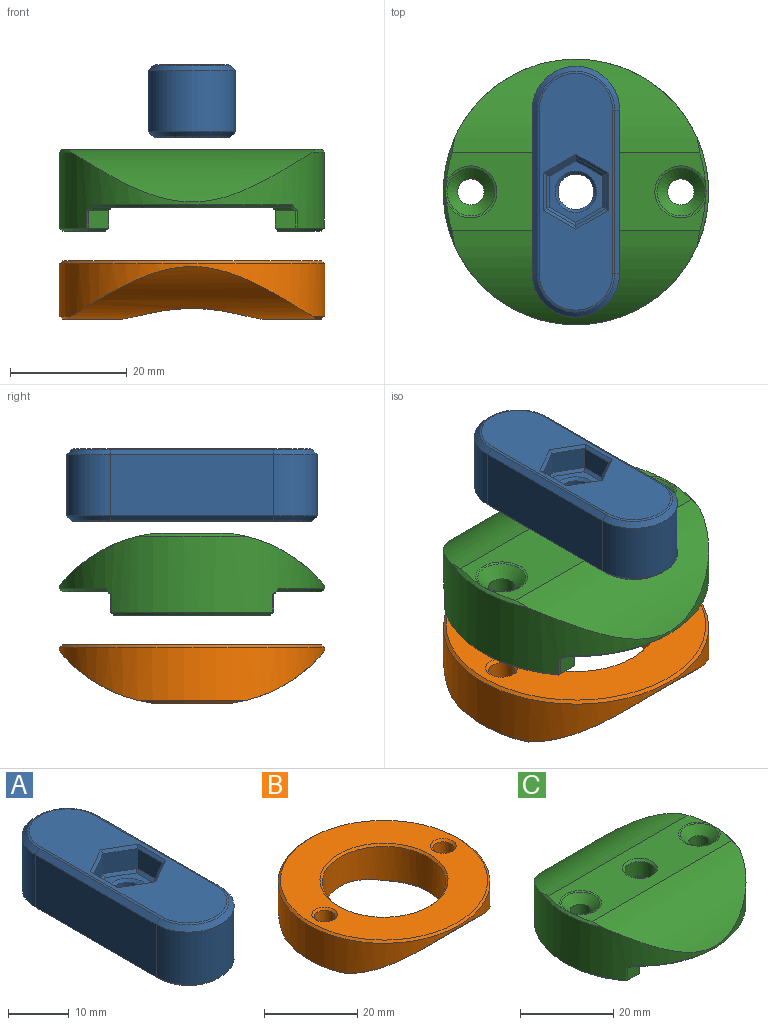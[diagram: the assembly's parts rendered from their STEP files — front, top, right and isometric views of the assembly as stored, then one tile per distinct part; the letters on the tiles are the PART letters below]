
ASSEMBLY  parts=3 mates=2
PART A: 44 faces, bbox 15x43x12.5 mm
  f0: plane 5.05x4mm, normal (-0.5,-0.87,0), area 23.3mm2, adj f1,f9,f35,f41
  f1: plane 5.83x4mm, normal (-1,0,0), area 23.3mm2, adj f0,f2,f36,f42
  f2: plane 5.05x4mm, normal (-0.5,0.87,0), area 23.3mm2, adj f1,f3,f34,f40
  f3: plane 5.05x4mm, normal (0.5,0.87,0), area 23.3mm2, adj f2,f4,f32,f38
  f4: plane 5.83x4mm, normal (1,0,0), area 23.3mm2, adj f3,f9,f31,f37
  f5: cylinder r=7.5mm len=15mm, axis (0,0,-1), area 247.4mm2, adj f6,f8,f15,f19
  f6: plane 28x10.5mm, normal (-1,0,0), area 294mm2, adj f5,f7,f14,f18
  f7: cylinder r=7.5mm len=15mm, axis (0,0,-1), area 247.4mm2, adj f6,f8,f16,f20
  f8: plane 28x10.5mm, normal (1,0,0), area 294mm2, adj f5,f7,f17,f21
  f9: plane 5.05x4mm, normal (0.5,-0.87,0), area 23.3mm2, adj f0,f4,f33,f39
  f10: plane 40.59x12.59mm, normal (0,0,1), area 370.1mm2, adj f27,f28,f29,f30,f31,f32,f33,f34
  f11: plane 40.59x12.59mm, normal (0,0,-1), area 437.2mm2, adj f22,f23,f24,f25,f26
  f12: cylinder r=3.05mm len=6.5mm, axis (0,0,-1), area 124.6mm2, adj f26,f43
  f13: plane 10.51x9.1mm, normal (0,0,1), area 32.1mm2, adj f37,f38,f39,f40,f41,f42,f43
  f14: plane 28x0.85mm, normal (-0.71,0,0.71), area 33.8mm2, adj f6,f15,f16,f27
  f15: cone r=6.5mm half-angle=45deg, axis (0,0,-1), area 26.8mm2, adj f5,f14,f17,f29
  f16: cone r=6.5mm half-angle=45deg, axis (0,0,-1), area 26.8mm2, adj f7,f14,f17,f28
  f17: plane 28x0.85mm, normal (0.71,0,0.71), area 33.8mm2, adj f8,f15,f16,f30
  f18: plane 28x0.85mm, normal (-0.71,0,-0.71), area 33.8mm2, adj f6,f19,f20,f22
  f19: cone r=7.5mm half-angle=45deg, axis (0,0,1), area 26.8mm2, adj f5,f18,f21,f23
  f20: cone r=7.5mm half-angle=45deg, axis (0,0,1), area 26.8mm2, adj f7,f18,f21,f24
  f21: plane 28x0.85mm, normal (0.71,0,-0.71), area 33.8mm2, adj f8,f19,f20,f25
  f22: plane 28x0.35mm, normal (-0.38,0,-0.92), area 10.7mm2, adj f11,f18,f23,f24
  f23: cone r=6.29mm half-angle=67.5deg, axis (0,0,1), area 7.8mm2, adj f11,f19,f22,f25
  f24: cone r=6.29mm half-angle=67.5deg, axis (0,0,1), area 7.8mm2, adj f11,f20,f22,f25
  f25: plane 28x0.35mm, normal (0.38,0,-0.92), area 10.7mm2, adj f11,f21,f23,f24
  f26: cone r=3.55mm half-angle=45deg, axis (0,0,-1), area 14.7mm2, adj f11,f12
  f27: plane 28x0.35mm, normal (-0.38,0,0.92), area 10.7mm2, adj f10,f14,f28,f29
  f28: cone r=6.29mm half-angle=67.5deg, axis (0,0,-1), area 7.8mm2, adj f10,f16,f27,f30
  f29: cone r=6.29mm half-angle=67.5deg, axis (0,0,-1), area 7.8mm2, adj f10,f15,f27,f30
  f30: plane 28x0.35mm, normal (0.38,0,0.92), area 10.7mm2, adj f10,f17,f28,f29
  f31: plane 6.41x0.5mm, normal (0.71,0,0.71), area 4.3mm2, adj f4,f10,f32,f33
  f32: plane 5.55x3.49mm, normal (0.35,0.61,0.71), area 4.3mm2, adj f3,f10,f31,f34
  f33: plane 5.55x3.49mm, normal (0.35,-0.61,0.71), area 4.3mm2, adj f9,f10,f31,f35
  f34: plane 5.55x3.49mm, normal (-0.35,0.61,0.71), area 4.3mm2, adj f2,f10,f32,f36
  f35: plane 5.55x3.49mm, normal (-0.35,-0.61,0.71), area 4.3mm2, adj f0,f10,f33,f36
  f36: plane 6.41x0.5mm, normal (-0.71,0,0.71), area 4.3mm2, adj f1,f10,f34,f35
  f37: plane 5.83x0.5mm, normal (0.71,0,0.71), area 3.9mm2, adj f4,f13,f38,f39
  f38: plane 5.05x3.2mm, normal (0.35,0.61,0.71), area 3.9mm2, adj f3,f13,f37,f40
  f39: plane 5.05x3.2mm, normal (0.35,-0.61,0.71), area 3.9mm2, adj f9,f13,f37,f41
  f40: plane 5.05x3.2mm, normal (-0.35,0.61,0.71), area 3.9mm2, adj f2,f13,f38,f42
  f41: plane 5.05x3.2mm, normal (-0.35,-0.61,0.71), area 3.9mm2, adj f0,f13,f39,f42
  f42: plane 5.83x0.5mm, normal (-0.71,0,0.71), area 3.9mm2, adj f1,f13,f40,f41
  f43: cone r=3.05mm half-angle=45deg, axis (0,0,1), area 14.7mm2, adj f12,f13
PART B: 57 faces, bbox 45.5x45.5x10 mm
  f0: cylinder r=22.75mm len=45.5mm, axis (0,0,1), area 795.7mm2, adj f4,f5,f41,f55,f56
  f1: cylinder r=13.25mm len=26.5mm, axis (0,0,1), area 714.6mm2, adj f6,f7,f42,f55,f56
  f2: plane 13.34x10.23mm, normal (0,0,-1), area 59.5mm2, adj f4,f7,f49,f50,f51,f52,f53,f54
  f3: plane 13.34x10.23mm, normal (0,0,-1), area 59.5mm2, adj f5,f6,f43,f44,f45,f46,f47,f48
  f4: cone r=22.75mm half-angle=45deg, axis (0,0,1), area 11.7mm2, adj f0,f2,f55,f56
  f5: cone r=22.75mm half-angle=45deg, axis (0,0,1), area 11.7mm2, adj f0,f3,f55,f56
  f6: cone r=13.75mm half-angle=45deg, axis (0,0,-1), area 12.2mm2, adj f1,f3,f55,f56
  f7: cone r=13.75mm half-angle=45deg, axis (0,0,-1), area 12.2mm2, adj f1,f2,f55,f56
  f8: plane 3.55x2.05mm, normal (-0.5,-0.87,0), area 8.2mm2, adj f9,f19,f36,f47
  f9: plane 4.1x2mm, normal (-1,0,0), area 8.2mm2, adj f8,f10,f37,f48
  f10: plane 3.55x2.05mm, normal (-0.5,0.87,0), area 8.2mm2, adj f9,f11,f35,f46
  f11: plane 3.55x2.05mm, normal (0.5,0.87,0), area 8.2mm2, adj f10,f12,f33,f44
  f12: plane 4.1x2mm, normal (1,0,0), area 8.2mm2, adj f11,f19,f32,f43
  f13: plane 3.55x2.05mm, normal (-0.5,-0.87,0), area 8.2mm2, adj f14,f18,f29,f53
  f14: plane 4.1x2mm, normal (-1,0,0), area 8.2mm2, adj f13,f15,f30,f54
  f15: plane 3.55x2.05mm, normal (-0.5,0.87,0), area 8.2mm2, adj f14,f16,f28,f52
  f16: plane 3.55x2.05mm, normal (0.5,0.87,0), area 8.2mm2, adj f15,f17,f26,f50
  f17: plane 4.1x2mm, normal (1,0,0), area 8.2mm2, adj f16,f18,f25,f49
  f18: plane 3.55x2.05mm, normal (0.5,-0.87,0), area 8.2mm2, adj f13,f17,f27,f51
  f19: plane 3.55x2.05mm, normal (0.5,-0.87,0), area 8.2mm2, adj f8,f12,f34,f45
  f20: plane 44.5x44.5mm, normal (0,0,1), area 913.8mm2, adj f39,f40,f41,f42
  f21: cylinder r=2.25mm len=6mm, axis (0,0,1), area 84.8mm2, adj f31,f40
  f22: plane 7.04x6.1mm, normal (0,0,-1), area 8.5mm2, adj f25,f26,f27,f28,f29,f30,f31
  f23: cylinder r=2.25mm len=6mm, axis (0,0,1), area 84.8mm2, adj f38,f39
  f24: plane 7.04x6.1mm, normal (0,0,-1), area 8.5mm2, adj f32,f33,f34,f35,f36,f37,f38
  f25: plane 4.1x0.5mm, normal (0.71,0,-0.71), area 2.7mm2, adj f17,f22,f26,f27
  f26: plane 3.55x2.34mm, normal (0.35,0.61,-0.71), area 2.7mm2, adj f16,f22,f25,f28
  f27: plane 3.55x2.34mm, normal (0.35,-0.61,-0.71), area 2.7mm2, adj f18,f22,f25,f29
  f28: plane 3.55x2.34mm, normal (-0.35,0.61,-0.71), area 2.7mm2, adj f15,f22,f26,f30
  f29: plane 3.55x2.34mm, normal (-0.35,-0.61,-0.71), area 2.7mm2, adj f13,f22,f27,f30
  f30: plane 4.1x0.5mm, normal (-0.71,0,-0.71), area 2.7mm2, adj f14,f22,f28,f29
  f31: cone r=2.75mm half-angle=45deg, axis (0,0,-1), area 11.1mm2, adj f21,f22
  f32: plane 4.1x0.5mm, normal (0.71,0,-0.71), area 2.7mm2, adj f12,f24,f33,f34
  f33: plane 3.55x2.34mm, normal (0.35,0.61,-0.71), area 2.7mm2, adj f11,f24,f32,f35
  f34: plane 3.55x2.34mm, normal (0.35,-0.61,-0.71), area 2.7mm2, adj f19,f24,f32,f36
  f35: plane 3.55x2.34mm, normal (-0.35,0.61,-0.71), area 2.7mm2, adj f10,f24,f33,f37
  f36: plane 3.55x2.34mm, normal (-0.35,-0.61,-0.71), area 2.7mm2, adj f8,f24,f34,f37
  f37: plane 4.1x0.5mm, normal (-0.71,0,-0.71), area 2.7mm2, adj f9,f24,f35,f36
  f38: cone r=2.75mm half-angle=45deg, axis (0,0,-1), area 11.1mm2, adj f23,f24
  f39: cone r=2.25mm half-angle=45deg, axis (0,0,1), area 11.1mm2, adj f20,f23
  f40: cone r=2.25mm half-angle=45deg, axis (0,0,1), area 11.1mm2, adj f20,f21
  f41: cone r=22.25mm half-angle=45deg, axis (0,0,-1), area 100mm2, adj f0,f20
  f42: cone r=13.25mm half-angle=45deg, axis (0,0,1), area 60mm2, adj f1,f20
  f43: plane 4.68x0.5mm, normal (0.71,0,-0.71), area 3.1mm2, adj f3,f12,f44,f45
  f44: plane 4.05x2.63mm, normal (0.35,0.61,-0.71), area 3.1mm2, adj f3,f11,f43,f46
  f45: plane 4.05x2.63mm, normal (0.35,-0.61,-0.71), area 3.1mm2, adj f3,f19,f43,f47
  f46: plane 4.05x2.63mm, normal (-0.35,0.61,-0.71), area 3.1mm2, adj f3,f10,f44,f48
  f47: plane 4.05x2.63mm, normal (-0.35,-0.61,-0.71), area 3.1mm2, adj f3,f8,f45,f48
  f48: plane 4.68x0.5mm, normal (-0.71,0,-0.71), area 3.1mm2, adj f3,f9,f46,f47
  f49: plane 4.68x0.5mm, normal (0.71,0,-0.71), area 3.1mm2, adj f2,f17,f50,f51
  f50: plane 4.05x2.63mm, normal (0.35,0.61,-0.71), area 3.1mm2, adj f2,f16,f49,f52
  f51: plane 4.05x2.63mm, normal (0.35,-0.61,-0.71), area 3.1mm2, adj f2,f18,f49,f53
  f52: plane 4.05x2.63mm, normal (-0.35,0.61,-0.71), area 3.1mm2, adj f2,f15,f50,f54
  f53: plane 4.05x2.63mm, normal (-0.35,-0.61,-0.71), area 3.1mm2, adj f2,f13,f51,f54
  f54: plane 4.68x0.5mm, normal (-0.71,0,-0.71), area 3.1mm2, adj f2,f14,f52,f53
  f55: cylinder r=25mm len=42.45mm, axis (1,0,0), area 465.5mm2, adj f0,f1,f2,f3,f4,f5,f6,f7
  f56: cylinder r=25mm len=42.45mm, axis (1,0,0), area 465.5mm2, adj f0,f1,f2,f3,f4,f5,f6,f7
PART C: 73 faces, bbox 45.5x45.5x14 mm
  f0: cylinder r=22.75mm len=45.5mm, axis (0,0,-1), area 1035.9mm2, adj f2,f3,f26,f29,f30,f33,f36,f38
  f1: plane 44.4x13.34mm, normal (0,0,1), area 416.3mm2, adj f2,f3,f60,f61,f62,f71,f72
  f2: cone r=22.25mm half-angle=45deg, axis (0,0,-1), area 11.6mm2, adj f0,f1,f60,f71,f72
  f3: cone r=22.25mm half-angle=45deg, axis (0,0,-1), area 11.4mm2, adj f0,f1,f61,f71,f72
  f4: plane 44.5x33.75mm, normal (0,0,-1), area 1053.9mm2, adj f32,f33,f35,f40,f41,f45,f48,f49
  f5: cylinder r=2.25mm len=11.5mm, axis (0,0,-1), area 162.6mm2, adj f23,f64
  f6: cylinder r=2.25mm len=11.5mm, axis (0,0,-1), area 162.6mm2, adj f24,f63
  f7: cylinder r=3.25mm len=6.5mm, axis (0,0,-1), area 81.7mm2, adj f59,f62
  f8: plane 5.83x4mm, normal (-1,0,0), area 23.3mm2, adj f9,f13,f58,f70
  f9: plane 5.05x4mm, normal (-0.5,-0.87,0), area 23.3mm2, adj f8,f10,f57,f69
  f10: plane 5.05x4mm, normal (0.5,-0.87,0), area 23.3mm2, adj f9,f11,f55,f67
  f11: plane 5.83x4mm, normal (1,0,0), area 23.3mm2, adj f10,f12,f53,f65
  f12: plane 5.05x4mm, normal (0.5,0.87,0), area 23.3mm2, adj f11,f13,f54,f66
  f13: plane 5.05x4mm, normal (-0.5,0.87,0), area 23.3mm2, adj f8,f12,f56,f68
  f14: plane 10.51x9.1mm, normal (0,0,-1), area 27.5mm2, adj f53,f54,f55,f56,f57,f58,f59
  f15: plane 28x3mm, normal (1,0,0), area 84mm2, adj f16,f17,f42,f45
  f16: plane 3.44x3mm, normal (0,1,0), area 10.3mm2, adj f15,f37,f38,f41
  f17: plane 3.44x3mm, normal (0,-1,0), area 10.3mm2, adj f15,f46,f49,f52
  f18: plane 27x7.5mm, normal (0,0,-1), area 139.5mm2, adj f37,f42,f46,f47,f63
  f19: plane 3.44x3mm, normal (0,1,0), area 10.3mm2, adj f20,f25,f26,f32
  f20: plane 28x3mm, normal (-1,0,0), area 84mm2, adj f19,f21,f28,f35
  f21: plane 3.44x3mm, normal (0,-1,0), area 10.3mm2, adj f20,f31,f39,f40
  f22: plane 27x7.5mm, normal (0,0,-1), area 139.5mm2, adj f25,f28,f30,f31,f64
  f23: cone r=2.25mm half-angle=45deg, axis (0,0,1), area 52.3mm2, adj f5,f61
  f24: cone r=2.25mm half-angle=45deg, axis (0,0,1), area 52.3mm2, adj f6,f60
  f25: plane 3.44x0.5mm, normal (0,0.71,-0.71), area 2.3mm2, adj f19,f22,f27,f28
  f26: plane 3x0.4mm, normal (0.44,0.9,0), area 1.3mm2, adj f0,f19,f27,f29
  f27: plane 0.5x0.5mm, normal (0.33,0.67,-0.67), area 0.1mm2, adj f25,f26,f30
  f28: plane 28x0.5mm, normal (-0.71,0,-0.71), area 19.4mm2, adj f20,f22,f25,f31
  f29: bspline ~1.22x1.04mm, area 0.6mm2, adj f0,f26,f32,f33
  f30: cone r=22.75mm half-angle=45deg, axis (0,0,1), area 20.7mm2, adj f0,f22,f27,f34
  f31: plane 3.44x0.5mm, normal (0,-0.71,-0.71), area 2.3mm2, adj f21,f22,f28,f34
  f32: plane 3.94x0.5mm, normal (0,0.71,-0.71), area 2.3mm2, adj f4,f19,f29,f35
  f33: cone r=22.75mm half-angle=45deg, axis (0,0,1), area 27.4mm2, adj f0,f4,f29,f36
  f34: plane 0.5x0.5mm, normal (0.33,-0.67,-0.67), area 0.1mm2, adj f30,f31,f39
  f35: plane 29x0.5mm, normal (-0.71,0,-0.71), area 20.2mm2, adj f4,f20,f32,f40
  f36: bspline ~1.21x1.02mm, area 0.6mm2, adj f0,f33,f38,f41
  f37: plane 3.44x0.5mm, normal (0,0.71,-0.71), area 2.3mm2, adj f16,f18,f42,f43
  f38: plane 3x0.4mm, normal (-0.44,0.9,0), area 1.3mm2, adj f0,f16,f36,f43
  f39: plane 3x0.4mm, normal (0.44,-0.9,0), area 1.3mm2, adj f0,f21,f34,f44
  f40: plane 3.94x0.5mm, normal (0,-0.71,-0.71), area 2.3mm2, adj f4,f21,f35,f44
  f41: plane 3.94x0.5mm, normal (0,0.71,-0.71), area 2.3mm2, adj f4,f16,f36,f45
  f42: plane 28x0.5mm, normal (0.71,0,-0.71), area 19.4mm2, adj f15,f18,f37,f46
  f43: plane 0.5x0.5mm, normal (-0.33,0.67,-0.67), area 0.1mm2, adj f37,f38,f47
  f44: bspline ~1.21x1.02mm, area 0.6mm2, adj f0,f39,f40,f48
  f45: plane 29x0.5mm, normal (0.71,0,-0.71), area 20.2mm2, adj f4,f15,f41,f49
  f46: plane 3.44x0.5mm, normal (0,-0.71,-0.71), area 2.3mm2, adj f17,f18,f42,f50
  f47: cone r=22.75mm half-angle=45deg, axis (0,0,1), area 20.7mm2, adj f0,f18,f43,f50
  f48: cone r=22.75mm half-angle=45deg, axis (0,0,1), area 27.4mm2, adj f0,f4,f44,f51
  f49: plane 3.94x0.5mm, normal (0,-0.71,-0.71), area 2.3mm2, adj f4,f17,f45,f51
  f50: plane 0.5x0.5mm, normal (-0.33,-0.67,-0.67), area 0.1mm2, adj f46,f47,f52
  f51: bspline ~1.22x1.04mm, area 0.6mm2, adj f0,f48,f49,f52
  f52: plane 3x0.4mm, normal (-0.44,-0.9,0), area 1.3mm2, adj f0,f17,f50,f51
  f53: plane 5.83x0.5mm, normal (0.71,0,-0.71), area 3.9mm2, adj f11,f14,f54,f55
  f54: plane 5.05x3.2mm, normal (0.35,0.61,-0.71), area 3.9mm2, adj f12,f14,f53,f56
  f55: plane 5.05x3.2mm, normal (0.35,-0.61,-0.71), area 3.9mm2, adj f10,f14,f53,f57
  f56: plane 5.05x3.2mm, normal (-0.35,0.61,-0.71), area 3.9mm2, adj f13,f14,f54,f58
  f57: plane 5.05x3.2mm, normal (-0.35,-0.61,-0.71), area 3.9mm2, adj f9,f14,f55,f58
  f58: plane 5.83x0.5mm, normal (-0.71,0,-0.71), area 3.9mm2, adj f8,f14,f56,f57
  f59: cone r=3.75mm half-angle=45deg, axis (0,0,-1), area 15.6mm2, adj f7,f14
  f60: cone r=4.46mm half-angle=67.5deg, axis (0,0,1), area 10mm2, adj f1,f2,f24
  f61: cone r=4.46mm half-angle=67.5deg, axis (0,0,1), area 10.1mm2, adj f1,f3,f23
  f62: cone r=3.25mm half-angle=45deg, axis (0,0,1), area 15.6mm2, adj f1,f7
  f63: cone r=2.75mm half-angle=45deg, axis (0,0,-1), area 11.1mm2, adj f6,f18
  f64: cone r=2.75mm half-angle=45deg, axis (0,0,-1), area 11.1mm2, adj f5,f22
  f65: plane 6.41x0.5mm, normal (0.71,0,-0.71), area 4.3mm2, adj f4,f11,f66,f67
  f66: plane 5.55x3.49mm, normal (0.35,0.61,-0.71), area 4.3mm2, adj f4,f12,f65,f68
  f67: plane 5.55x3.49mm, normal (0.35,-0.61,-0.71), area 4.3mm2, adj f4,f10,f65,f69
  f68: plane 5.55x3.49mm, normal (-0.35,0.61,-0.71), area 4.3mm2, adj f4,f13,f66,f70
  f69: plane 5.55x3.49mm, normal (-0.35,-0.61,-0.71), area 4.3mm2, adj f4,f9,f67,f70
  f70: plane 6.41x0.5mm, normal (-0.71,0,-0.71), area 4.3mm2, adj f4,f8,f68,f69
  f71: cylinder r=25mm len=42.45mm, axis (1,0,0), area 577.7mm2, adj f0,f1,f2,f3
  f72: cylinder r=25mm len=42.45mm, axis (1,0,0), area 577.7mm2, adj f0,f1,f2,f3
PLACE A t=(-36.94,-1.52,52.8)mm
PLACE B t=(-36.94,-1.52,31.67)mm
PLACE C t=(-36.94,-1.52,40.8)mm
MATE slider B.f1 <-> C.f0  axis (0,0,1) through (-36.94,-1.52,31.67)mm
MATE revolute A.f12 <-> C.f7  axis (0,0,-1) through (-36.94,-1.52,52.8)mm
